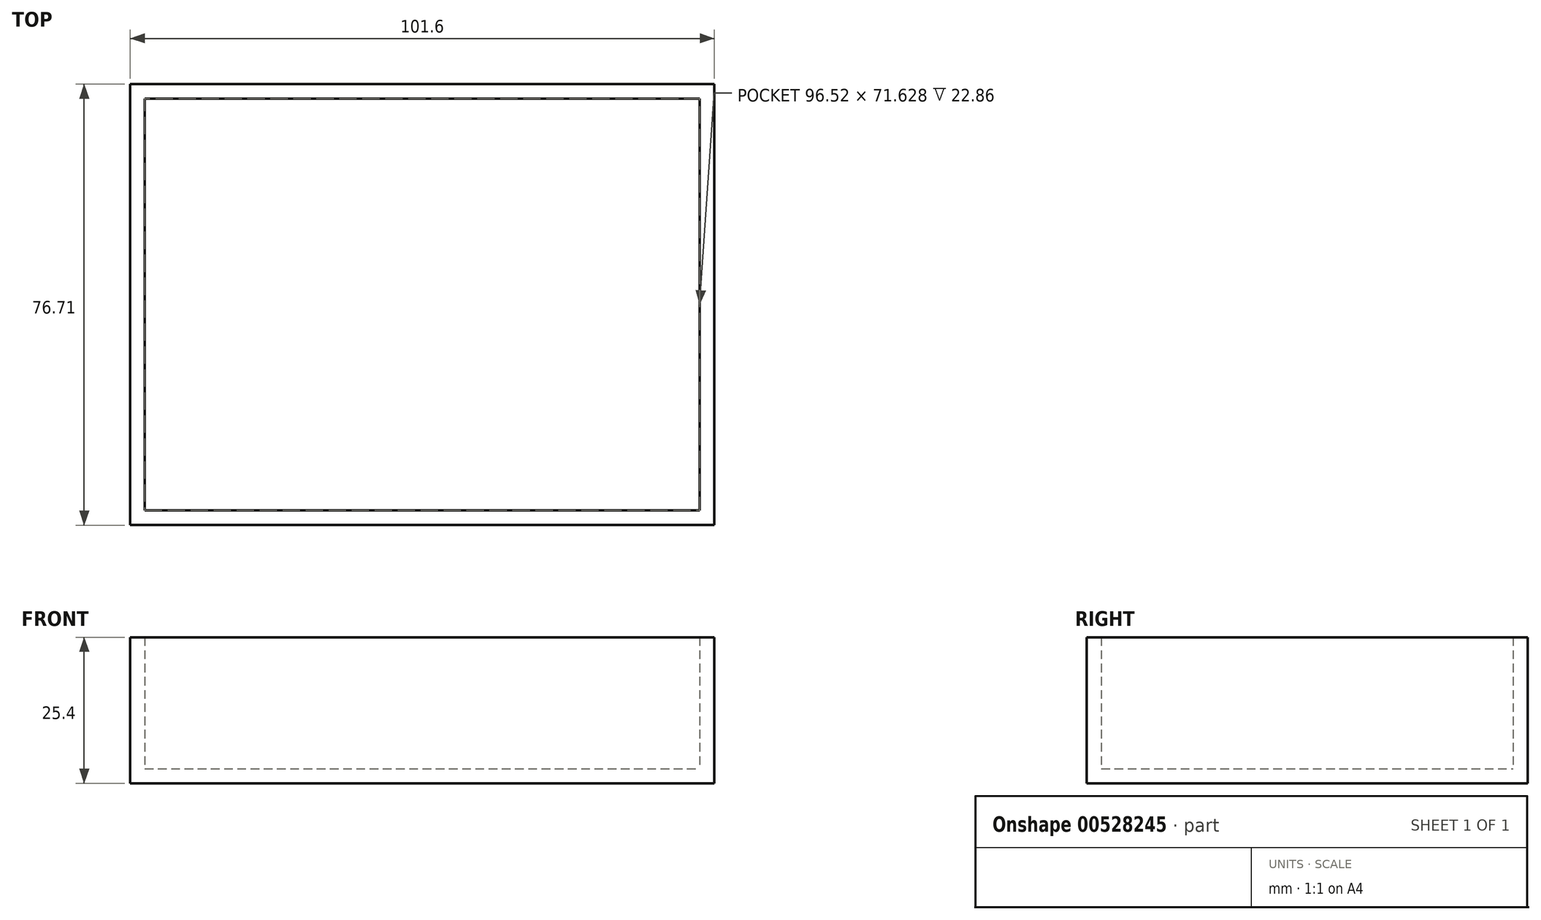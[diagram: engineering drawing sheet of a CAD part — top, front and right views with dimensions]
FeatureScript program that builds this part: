
annotation { "Feature Type Name" : "Feature", "Feature Type Description" : "" }
export const myFeature = defineFeature(function(context is Context, id is Id, definition is map)
    precondition{}
    {
        {
            var Q0;
            Q0=qCreatedBy(makeId("Front.planeOp"),FACE);
            var sketch = newSketch(context, id + "F0", { "sketchPlane" : qUnion([Q0])});
            skLineSegment(sketch, "E0.bottom", {"start": v(0, 0) * mm, "end": v(101.6, 0) * mm});
            skLineSegment(sketch, "E0.top", {"start": v(0, -25.4) * mm, "end": v(101.6, -25.4) * mm});
            skLineSegment(sketch, "E0.left", {"start": v(0, 0) * mm, "end": v(0, -25.4) * mm});
            skLineSegment(sketch, "E0.right", {"start": v(101.6, 0) * mm, "end": v(101.6, -25.4) * mm});
            skSolve(sketch);
        }
        {
            var Q0;
            Q0=makeQuery(id+"F0.imprint","IMPRINT",FACE,{"disambiguationData":[TD([[makeQuery(id+"F0.imprint","IMPRINT",EDGE,{"derivedFrom":sQuery(id+"F0.wireOp",EDGE,"E0.bottom")}),-1.0]])]});
            extrude(context, id + "F1", {"entities" : qUnion([Q0]), "depth" : 76.7 * mm, "offsetDistance" : 25.4 * mm});
        }
        {
            var Q0;
            Q0=makeQuery(id+"F1.opExtrude","SWEPT_FACE",FACE,{"disambiguationData":[OSD([sQuery(id+"F0.wireOp",EDGE,"E0.bottom")])]});
            shell(context, id + "F2", {"entities" : qUnion([Q0]), "thickness" : 2.54 * mm});
        }
    });
